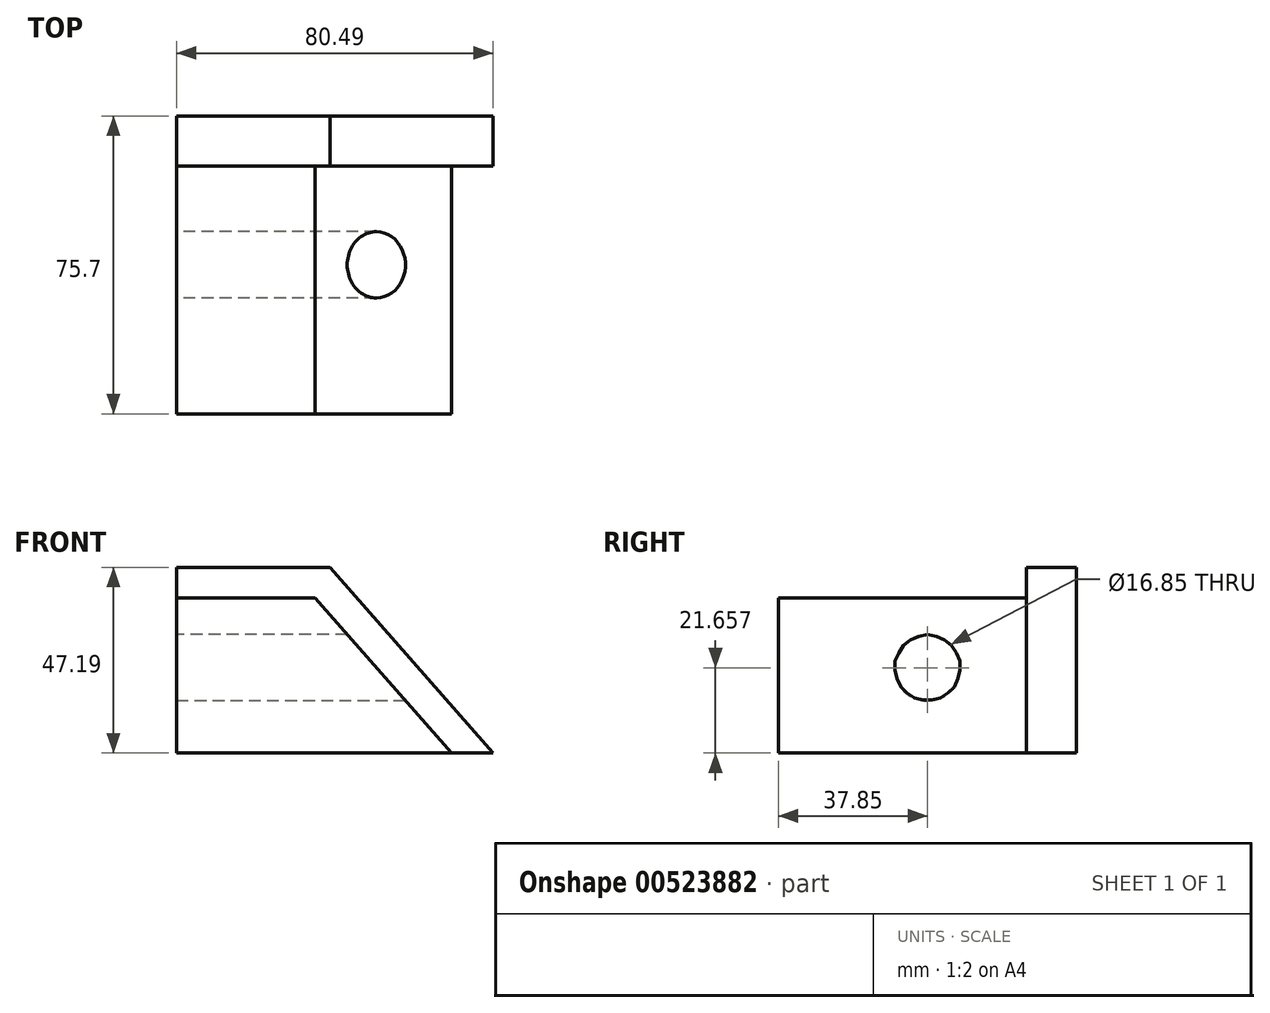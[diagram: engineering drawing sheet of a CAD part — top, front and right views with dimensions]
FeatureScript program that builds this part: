
annotation { "Feature Type Name" : "Feature", "Feature Type Description" : "" }
export const myFeature = defineFeature(function(context is Context, id is Id, definition is map)
    precondition{}
    {
        {
            var Q0;
            Q0=qCreatedBy(makeId("Front.planeOp"),FACE);
            var sketch = newSketch(context, id + "F0", { "sketchPlane" : qUnion([Q0])});
            skLineSegment(sketch, "E0", {"start": v(-47.18, 0) * mm, "end": v(-47.18, 47.2) * mm});
            skLineSegment(sketch, "E1", {"start": v(-47.18, 47.2) * mm, "end": v(-8.19, 47.2) * mm});
            skLineSegment(sketch, "E2", {"start": v(-8.19, 47.2) * mm, "end": v(33.3, 0) * mm});
            skLineSegment(sketch, "E3", {"start": v(33.3, 0) * mm, "end": v(-47.18, 0) * mm});
            skSolve(sketch);
        }
        {
            var Q0;
            Q0=makeQuery(id+"F0.imprint","IMPRINT",FACE,{"disambiguationData":[TD([[makeQuery(id+"F0.imprint","IMPRINT",EDGE,{"derivedFrom":sQuery(id+"F0.wireOp",EDGE,"E0")}),-1.0]])]});
            extrude(context, id + "F1", {"entities" : qUnion([Q0]), "endBound" : BoundingType.SYMMETRIC, "depth" : 75.7 * mm, "offsetDistance" : 25.4 * mm});
        }
        {
            var Q0;
            Q0=makeQuery(id+"F1.opExtrude","CAP_FACE",FACE,{"disambiguationData":[OSD([sQuery(id+"F0.wireOp",EDGE,"E0"),sQuery(id+"F0.wireOp",EDGE,"E1"),sQuery(id+"F0.wireOp",EDGE,"E2"),sQuery(id+"F0.wireOp",EDGE,"E3")])],"isStart":false});
            var sketch = newSketch(context, id + "F2", { "sketchPlane" : qUnion([Q0])});
            skLineSegment(sketch, "E4", {"start": v(-47.18, 39.38) * mm, "end": v(-11.97, 39.38) * mm});
            skLineSegment(sketch, "E5", {"start": v(-11.97, 39.38) * mm, "end": v(22.7, 0) * mm});
            skLineSegment(sketch, "E6", {"start": v(22.7, 0) * mm, "end": v(33.3, 0) * mm});
            skLineSegment(sketch, "E7", {"start": v(33.3, 0) * mm, "end": v(-8.19, 47.2) * mm});
            skLineSegment(sketch, "E8", {"start": v(-8.19, 47.2) * mm, "end": v(-47.18, 47.2) * mm});
            skLineSegment(sketch, "E9", {"start": v(-47.18, 47.2) * mm, "end": v(-47.18, 39.38) * mm});
            skSolve(sketch);
        }
        {
            var Q0;
            Q0=makeQuery(id+"F2.imprint","IMPRINT",FACE,{"disambiguationData":[TD([[makeQuery(id+"F2.imprint","IMPRINT",EDGE,{"derivedFrom":sQuery(id+"F2.wireOp",EDGE,"E4")}),1.0]])]});
            extrude(context, id + "F3", {"entities" : qUnion([Q0]), "operationType" : NewBodyOperationType.REMOVE, "oppositeDirection" : true, "depth" : 63 * mm, "offsetDistance" : 25.4 * mm});
        }
        {
            var Q0;
            Q0=makeQuery(id+"F1.opExtrude","SWEPT_FACE",FACE,{"disambiguationData":[OSD([sQuery(id+"F0.wireOp",EDGE,"E0")])]});
            var sketch = newSketch(context, id + "F4", { "sketchPlane" : qUnion([Q0])});
            skCircle(sketch, "E10", {"center": v(0, 21.66) * mm, "radius": 8.43 * mm});
            skSolve(sketch);
        }
        {
            var Q0;
            Q0=makeQuery(id+"F4.imprint","IMPRINT",FACE,{"disambiguationData":[TD([[makeQuery(id+"F4.imprint","IMPRINT",EDGE,{"derivedFrom":sQuery(id+"F4.wireOp",EDGE,"E10")}),1.0]])]});
            extrude(context, id + "F5", {"entities" : qUnion([Q0]), "operationType" : NewBodyOperationType.REMOVE, "oppositeDirection" : true, "depth" : 74.17 * mm, "offsetDistance" : 25.4 * mm});
        }
    });
